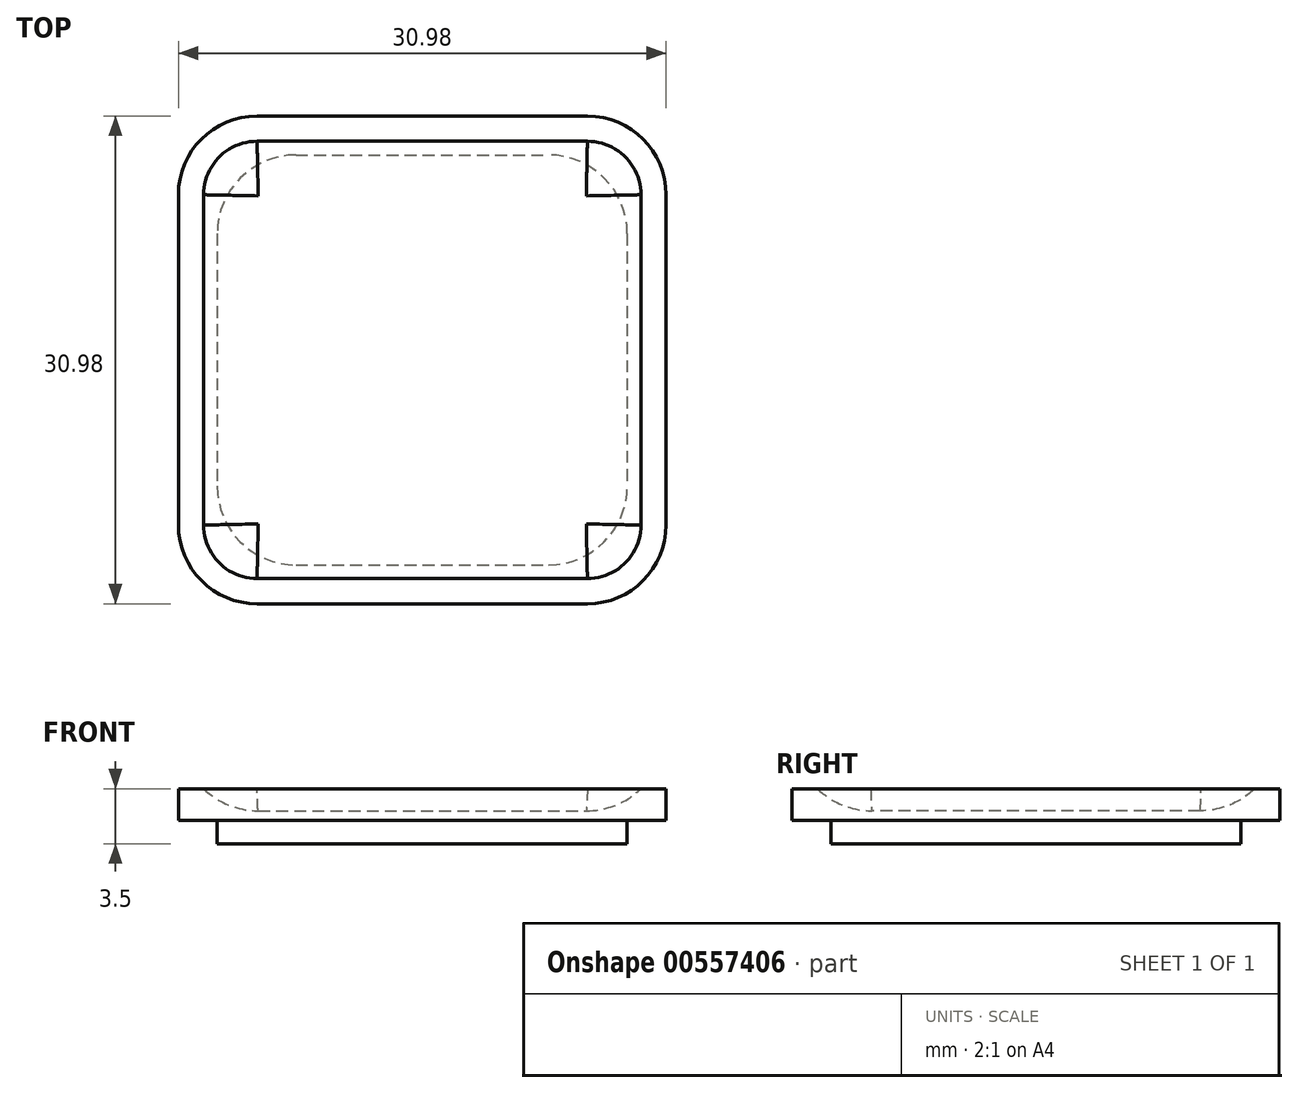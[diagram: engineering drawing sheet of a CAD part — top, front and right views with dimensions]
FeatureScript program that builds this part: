
annotation { "Feature Type Name" : "Feature", "Feature Type Description" : "" }
export const myFeature = defineFeature(function(context is Context, id is Id, definition is map)
    precondition{}
    {
        {
            var Q0;
            Q0=qCreatedBy(makeId("Top.planeOp"),FACE);
            var sketch = newSketch(context, id + "F0", { "sketchPlane" : qUnion([Q0])});
            skLineSegment(sketch, "E0.bottom", {"start": v(-15, 20) * mm, "end": v(20, 20) * mm, "construction": true});
            skLineSegment(sketch, "E0.top", {"start": v(-15, -15) * mm, "end": v(20, -15) * mm, "construction": true});
            skLineSegment(sketch, "E0.left", {"start": v(-15, 20) * mm, "end": v(-15, -15) * mm, "construction": true});
            skLineSegment(sketch, "E0.right", {"start": v(20, 20) * mm, "end": v(20, -15) * mm, "construction": true});
            skLineSegment(sketch, "E1.0", {"start": v(-13, 18) * mm, "end": v(18, 18) * mm});
            skLineSegment(sketch, "E1.1", {"start": v(-13, 18) * mm, "end": v(-13, -13) * mm});
            skLineSegment(sketch, "E1.2", {"start": v(-13, -13) * mm, "end": v(18, -13) * mm});
            skLineSegment(sketch, "E1.3", {"start": v(18, 18) * mm, "end": v(18, -13) * mm});
            skSolve(sketch);
        }
        {
            var Q0;
            Q0=qSketchRegion(id+"F0",true);
            extrude(context, id + "F1", {"entities" : qUnion([Q0]), "depth" : 2 * mm, "offsetDistance" : 25 * mm});
        }
        {
            var Q0;
            Q0=makeQuery(id+"F1.opExtrude","SWEPT_EDGE",EDGE,{"disambiguationData":[OSD([sQuery(id+"F0.wireOp",EDGE,"E1.1"),sQuery(id+"F0.wireOp",EDGE,"E1.2")])]});
            var Q1;
            Q1=makeQuery(id+"F1.opExtrude","SWEPT_EDGE",EDGE,{"disambiguationData":[OSD([sQuery(id+"F0.wireOp",EDGE,"E1.2"),sQuery(id+"F0.wireOp",EDGE,"E1.3")])]});
            var Q2;
            Q2=makeQuery(id+"F1.opExtrude","SWEPT_EDGE",EDGE,{"disambiguationData":[OSD([sQuery(id+"F0.wireOp",EDGE,"E1.0"),sQuery(id+"F0.wireOp",EDGE,"E1.3")])]});
            var Q3;
            Q3=makeQuery(id+"F1.opExtrude","SWEPT_EDGE",EDGE,{"disambiguationData":[OSD([sQuery(id+"F0.wireOp",EDGE,"E1.0"),sQuery(id+"F0.wireOp",EDGE,"E1.1")])]});
            fillet(context, id + "F2", {"entities" : qUnion([Q0, Q1, Q2, Q3]), "radius" : 5 * mm, "tangentPropagation" : true, "allowEdgeOverflow" : false});
        }
        {
            var Q0;
            Q0=makeQuery(id+"F1.opExtrude","CAP_FACE",FACE,{"disambiguationData":[OSD([sQuery(id+"F0.wireOp",EDGE,"E1.0"),sQuery(id+"F0.wireOp",EDGE,"E1.1"),sQuery(id+"F0.wireOp",EDGE,"E1.2"),sQuery(id+"F0.wireOp",EDGE,"E1.3")])],"isStart":true});
            var sketch = newSketch(context, id + "F3", { "sketchPlane" : qUnion([Q0])});
            skLineSegment(sketch, "E2.0", {"start": v(15.52, -15.52) * mm, "end": v(15.52, 10.52) * mm});
            skLineSegment(sketch, "E2.1", {"start": v(-10.52, -15.52) * mm, "end": v(15.52, -15.52) * mm});
            skLineSegment(sketch, "E2.2", {"start": v(-10.52, -15.52) * mm, "end": v(-10.52, 10.52) * mm});
            skLineSegment(sketch, "E2.3", {"start": v(-10.52, 10.52) * mm, "end": v(15.52, 10.52) * mm});
            skSolve(sketch);
        }
        {
            var Q0;
            Q0=qSketchRegion(id+"F3",true);
            extrude(context, id + "F4", {"entities" : qUnion([Q0]), "operationType" : NewBodyOperationType.ADD, "depth" : 1.5 * mm, "offsetDistance" : 25 * mm});
        }
        {
            var Q0;
            Q0=makeQuery(id+"F4.opExtrude","SWEPT_EDGE",EDGE,{"disambiguationData":[OSD([sQuery(id+"F3.wireOp",EDGE,"E2.0"),sQuery(id+"F3.wireOp",EDGE,"E2.3")])]});
            var Q1;
            Q1=makeQuery(id+"F4.opExtrude","SWEPT_EDGE",EDGE,{"disambiguationData":[OSD([sQuery(id+"F3.wireOp",EDGE,"E2.2"),sQuery(id+"F3.wireOp",EDGE,"E2.3")])]});
            var Q2;
            Q2=makeQuery(id+"F4.opExtrude","SWEPT_EDGE",EDGE,{"disambiguationData":[OSD([sQuery(id+"F3.wireOp",EDGE,"E2.0"),sQuery(id+"F3.wireOp",EDGE,"E2.1")])]});
            var Q3;
            Q3=makeQuery(id+"F4.opExtrude","SWEPT_EDGE",EDGE,{"disambiguationData":[OSD([sQuery(id+"F3.wireOp",EDGE,"E2.1"),sQuery(id+"F3.wireOp",EDGE,"E2.2")])]});
            fillet(context, id + "F5", {"entities" : qUnion([Q0, Q1, Q2, Q3]), "radius" : 5 * mm, "tangentPropagation" : true, "allowEdgeOverflow" : false});
        }
        {
            var Q0;
            Q0=makeQuery(id+"F1.opExtrude","CAP_FACE",FACE,{"disambiguationData":[OSD([sQuery(id+"F0.wireOp",EDGE,"E1.0"),sQuery(id+"F0.wireOp",EDGE,"E1.1"),sQuery(id+"F0.wireOp",EDGE,"E1.2"),sQuery(id+"F0.wireOp",EDGE,"E1.3")])],"isStart":false});
            var sketch = newSketch(context, id + "F6", { "sketchPlane" : qUnion([Q0])});
            skLineSegment(sketch, "E3.0", {"start": v(-8, 16.4) * mm, "end": v(13, 16.4) * mm});
            skArc(sketch, "E3.1", {"start": v(16.4, 13) * mm, "mid": v(15.4, 15.4) * mm, "end": v(13, 16.4) * mm});
            skArc(sketch, "E3.2", {"start": v(-8, 16.4) * mm, "mid": v(-10.4, 15.4) * mm, "end": v(-11.4, 13) * mm});
            skLineSegment(sketch, "E3.3", {"start": v(16.4, 13) * mm, "end": v(16.4, -8) * mm});
            skLineSegment(sketch, "E3.4", {"start": v(-11.4, 13) * mm, "end": v(-11.4, -8) * mm});
            skArc(sketch, "E3.5", {"start": v(-11.4, -8) * mm, "mid": v(-10.4, -10.4) * mm, "end": v(-8, -11.4) * mm});
            skLineSegment(sketch, "E3.6", {"start": v(-8, -11.4) * mm, "end": v(13, -11.4) * mm});
            skArc(sketch, "E3.7", {"start": v(13, -11.4) * mm, "mid": v(15.4, -10.4) * mm, "end": v(16.4, -8) * mm});
            skSolve(sketch);
        }
        {
            var Q0;
            Q0=makeQuery(id+"F6.imprint","IMPRINT",FACE,{"disambiguationData":[TD([[makeQuery(id+"F6.imprint","IMPRINT",EDGE,{"derivedFrom":sQuery(id+"F6.wireOp",EDGE,"E3.0")}),-1.0]])]});
            extrude(context, id + "F7", {"entities" : qUnion([Q0]), "operationType" : NewBodyOperationType.REMOVE, "oppositeDirection" : true, "depth" : 1.4 * mm, "offsetDistance" : 25 * mm});
        }
        {
            var Q0;
            Q0=makeQuery(id+"F7.boolean.opBoolean","COPY",EDGE,{"derivedFrom":makeQuery(id+"F7.opExtrude","CAP_EDGE",EDGE,{"disambiguationData":[OSD([sQuery(id+"F6.wireOp",EDGE,"E3.2")])],"isStart":false})});
            var Q1;
            Q1=makeQuery(id+"F7.boolean.opBoolean","COPY",FACE,{"derivedFrom":makeQuery(id+"F7.opExtrude","CAP_FACE",FACE,{"disambiguationData":[OSD([sQuery(id+"F6.wireOp",EDGE,"E3.0"),sQuery(id+"F6.wireOp",EDGE,"E3.1"),sQuery(id+"F6.wireOp",EDGE,"E3.2"),sQuery(id+"F6.wireOp",EDGE,"E3.3"),sQuery(id+"F6.wireOp",EDGE,"E3.4"),sQuery(id+"F6.wireOp",EDGE,"E3.5"),sQuery(id+"F6.wireOp",EDGE,"E3.6"),sQuery(id+"F6.wireOp",EDGE,"E3.7")])],"isStart":false})});
            fillet(context, id + "F8", {"entities" : qUnion([Q0, Q1]), "radius" : 5 * mm, "tangentPropagation" : true, "allowEdgeOverflow" : false});
        }
    });
